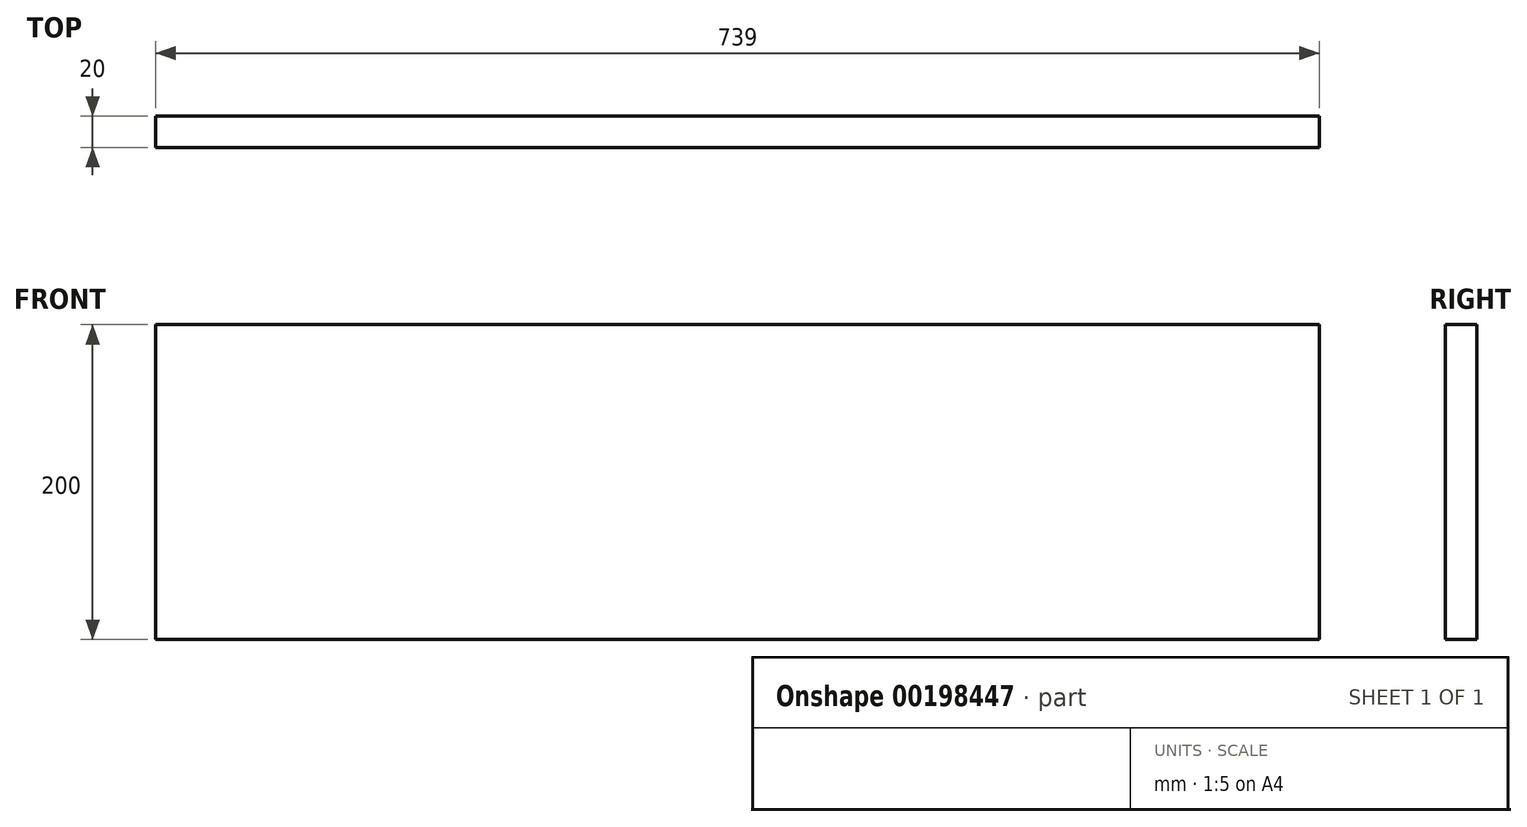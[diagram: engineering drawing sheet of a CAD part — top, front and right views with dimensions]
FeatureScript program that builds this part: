
annotation { "Feature Type Name" : "Feature", "Feature Type Description" : "" }
export const myFeature = defineFeature(function(context is Context, id is Id, definition is map)
    precondition{}
    {
        {
            var Q0;
            Q0=qCreatedBy(makeId("Top.planeOp"),FACE);
            var sketch = newSketch(context, id + "F0", { "sketchPlane" : qUnion([Q0])});
            skLineSegment(sketch, "E0.bottom", {"start": v(0, 0) * mm, "end": v(739, 0) * mm});
            skLineSegment(sketch, "E0.top", {"start": v(0, 20) * mm, "end": v(739, 20) * mm});
            skLineSegment(sketch, "E0.left", {"start": v(0, 0) * mm, "end": v(0, 20) * mm});
            skLineSegment(sketch, "E0.right", {"start": v(739, 0) * mm, "end": v(739, 20) * mm});
            skSolve(sketch);
        }
        {
            var Q0;
            Q0 = qSketchRegion(id + "F0", true);
            extrude(context, id + "F1", {"entities" : qUnion([Q0]), "depth" : 200 * mm});
        }
    });
